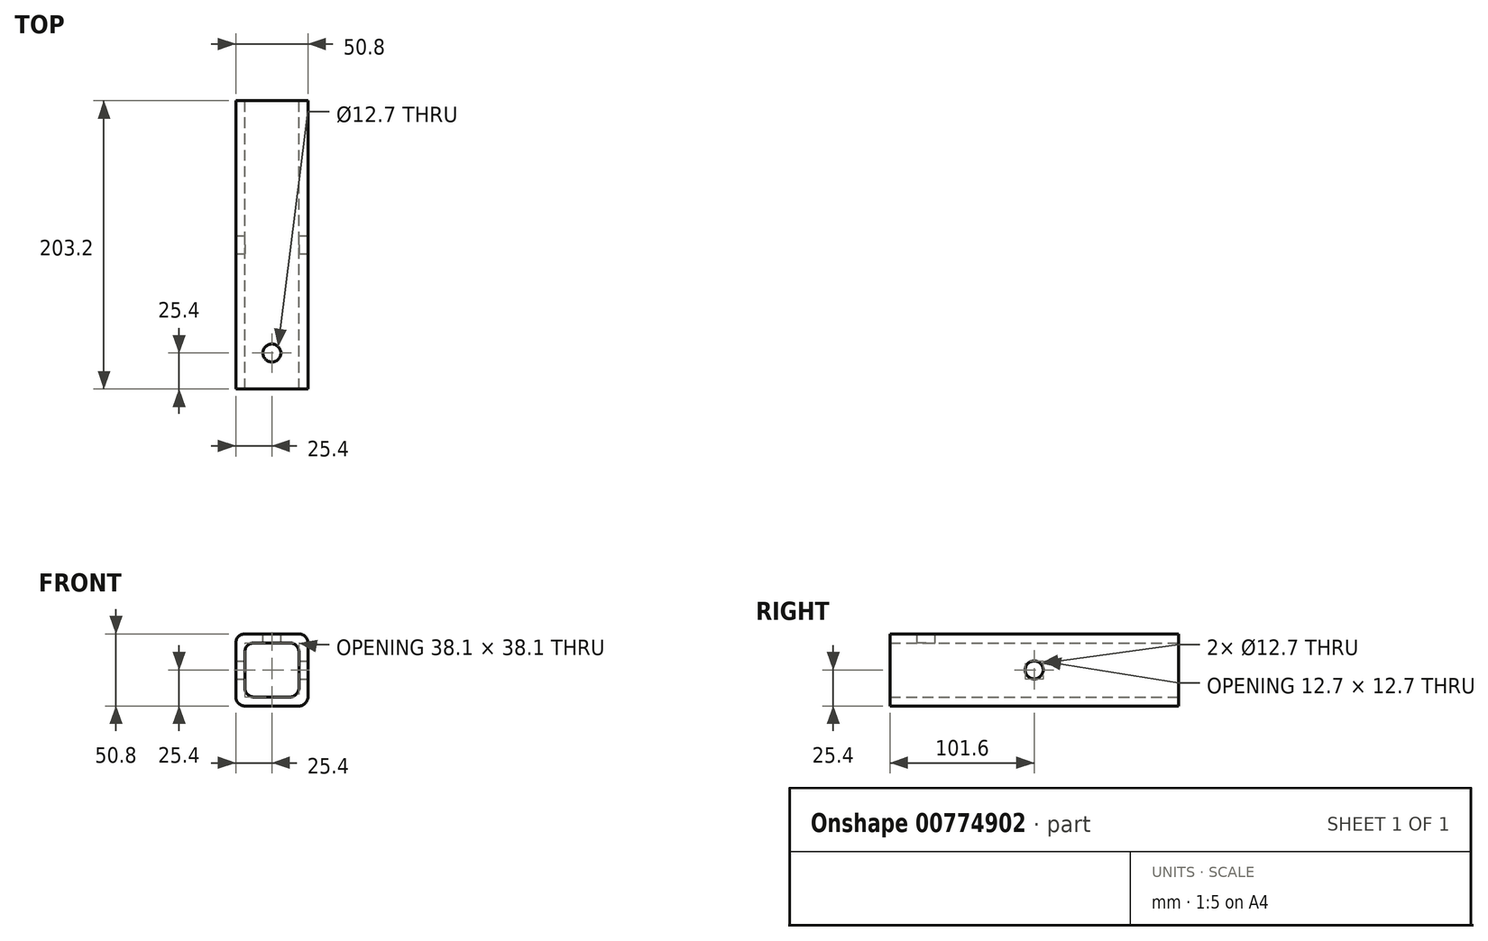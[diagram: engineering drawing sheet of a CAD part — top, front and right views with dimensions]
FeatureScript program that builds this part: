
annotation { "Feature Type Name" : "Feature", "Feature Type Description" : "" }
export const myFeature = defineFeature(function(context is Context, id is Id, definition is map)
    precondition{}
    {
        {
            var Q0;
            Q0=qCreatedBy(makeId("Front.planeOp"),FACE);
            var sketch = newSketch(context, id + "F0", { "sketchPlane" : qUnion([Q0])});
            skLineSegment(sketch, "E0.bottom", {"start": v(19.05, -25.4) * mm, "end": v(-19.05, -25.4) * mm});
            skLineSegment(sketch, "E0.top", {"start": v(19.05, 25.4) * mm, "end": v(-19.05, 25.4) * mm});
            skLineSegment(sketch, "E0.left", {"start": v(25.4, -19.05) * mm, "end": v(25.4, 19.05) * mm});
            skLineSegment(sketch, "E0.right", {"start": v(-25.4, -19.05) * mm, "end": v(-25.4, 19.05) * mm});
            skPoint(sketch, "E0.middle", {"position": v(0, 0) * mm});
            skLineSegment(sketch, "E1.bottom", {"start": v(12.7, -19.05) * mm, "end": v(-12.7, -19.05) * mm});
            skLineSegment(sketch, "E1.top", {"start": v(12.7, 19.05) * mm, "end": v(-12.7, 19.05) * mm});
            skLineSegment(sketch, "E1.left", {"start": v(19.05, -12.7) * mm, "end": v(19.05, 12.7) * mm});
            skLineSegment(sketch, "E1.right", {"start": v(-19.05, -12.7) * mm, "end": v(-19.05, 12.7) * mm});
            skPoint(sketch, "E2.visualSharp", {"position": v(-25.4, 25.4) * mm});
            skArc(sketch, "E2.filletArc", {"start": v(-19.05, 25.4) * mm, "mid": v(-23.54, 23.54) * mm, "end": v(-25.4, 19.05) * mm});
            skPoint(sketch, "E3.visualSharp", {"position": v(-25.4, -25.4) * mm});
            skArc(sketch, "E3.filletArc", {"start": v(-25.4, -19.05) * mm, "mid": v(-23.54, -23.54) * mm, "end": v(-19.05, -25.4) * mm});
            skPoint(sketch, "E4.visualSharp", {"position": v(25.4, -25.4) * mm});
            skArc(sketch, "E4.filletArc", {"start": v(19.05, -25.4) * mm, "mid": v(23.54, -23.54) * mm, "end": v(25.4, -19.05) * mm});
            skPoint(sketch, "E5.visualSharp", {"position": v(25.4, 25.4) * mm});
            skArc(sketch, "E5.filletArc", {"start": v(25.4, 19.05) * mm, "mid": v(23.54, 23.54) * mm, "end": v(19.05, 25.4) * mm});
            skArc(sketch, "E6.filletArc", {"start": v(12.7, -19.05) * mm, "mid": v(17.2, -17.2) * mm, "end": v(19.05, -12.7) * mm});
            skArc(sketch, "E7.filletArc", {"start": v(-19.05, -12.7) * mm, "mid": v(-17.2, -17.2) * mm, "end": v(-12.7, -19.05) * mm});
            skArc(sketch, "E8.filletArc", {"start": v(19.05, 12.7) * mm, "mid": v(17.2, 17.2) * mm, "end": v(12.7, 19.05) * mm});
            skArc(sketch, "E9.filletArc", {"start": v(-12.7, 19.05) * mm, "mid": v(-17.2, 17.2) * mm, "end": v(-19.05, 12.7) * mm});
            skSolve(sketch);
        }
        {
            var Q0;
            Q0=makeQuery(id+"F0.imprint","IMPRINT",FACE,{"disambiguationData":[TD([[makeQuery(id+"F0.imprint","IMPRINT",EDGE,{"derivedFrom":sQuery(id+"F0.wireOp",EDGE,"E0.bottom")}),-1.0]])]});
            extrude(context, id + "F1", {"entities" : qUnion([Q0]), "depth" : 203.2 * mm, "offsetDistance" : 25.4 * mm});
        }
        {
            var Q0;
            Q0=makeQuery(id+"F1.opExtrude","SWEPT_FACE",FACE,{"disambiguationData":[OSD([sQuery(id+"F0.wireOp",EDGE,"E0.left")])]});
            var sketch = newSketch(context, id + "F2", { "sketchPlane" : qUnion([Q0])});
            skCircle(sketch, "E10", {"center": v(-101.6, 0) * mm, "radius": 6.35 * mm});
            skSolve(sketch);
        }
        {
            var Q0;
            Q0=makeQuery(id+"F2.imprint","IMPRINT",FACE,{"disambiguationData":[TD([[makeQuery(id+"F2.imprint","IMPRINT",EDGE,{"derivedFrom":sQuery(id+"F2.wireOp",EDGE,"E10")}),1.0]])]});
            extrude(context, id + "F3", {"entities" : qUnion([Q0]), "operationType" : NewBodyOperationType.REMOVE, "oppositeDirection" : true, "depth" : 50.8 * mm, "offsetDistance" : 25.4 * mm});
        }
        {
            var Q0;
            Q0=makeQuery(id+"F1.opExtrude","SWEPT_FACE",FACE,{"disambiguationData":[OSD([sQuery(id+"F0.wireOp",EDGE,"E0.top")])]});
            var sketch = newSketch(context, id + "F4", { "sketchPlane" : qUnion([Q0])});
            skCircle(sketch, "E11", {"center": v(0, -177.8) * mm, "radius": 6.35 * mm});
            skSolve(sketch);
        }
        {
            var Q0;
            Q0=makeQuery(id+"F4.imprint","IMPRINT",FACE,{"disambiguationData":[TD([[makeQuery(id+"F4.imprint","IMPRINT",EDGE,{"derivedFrom":sQuery(id+"F4.wireOp",EDGE,"E11")}),1.0]])]});
            extrude(context, id + "F5", {"entities" : qUnion([Q0]), "operationType" : NewBodyOperationType.REMOVE, "oppositeDirection" : true, "depth" : 25.4 * mm, "offsetDistance" : 25.4 * mm});
        }
    });
